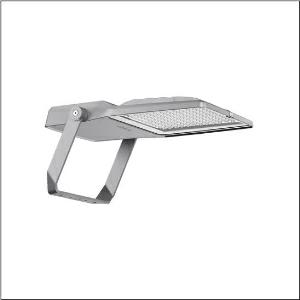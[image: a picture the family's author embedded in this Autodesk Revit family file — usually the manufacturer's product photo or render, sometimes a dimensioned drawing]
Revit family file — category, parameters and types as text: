
# Revit family: floodlight_fl_21_iq_midi___rs07_5xa7782f1b1a_00ed
name_source: partatom
category: Lighting Fixtures
units: mm (PartAtom-declared; Revit-internal decimal feet)

## family parameters
Cut with Voids When Loaded = No
Host = Face
Light Source = No
Part Type = Normal
Room Calculation Point = No
Round Connector Dimension = Use Diameter
Shared = No

## types (1)
- --- (1 x LED, 29450 lm, 270.2 W, 2200K)
    Apparent Load = 270 VA
    CIE Flux Codes = 79 92 99 100 100
    Color Rendering = 70
    Color Temperature = 2200K
    Default Elevation = 1800 mm
    Description = Floodlight FL 21 iQ midi, floodlight, primary light control with lens, of PMMA, primary optical cover: protective disc, of toughened safety glass, transparent, light distribution: RS07, light emission: direct distribution, installation type: surface-mounted, LED, High Power LED, rated luminous flux: 29.450lm, luminous efficacy: 109lm/W, light colour: 722, colour temperature: 2200K, control gear: ECG iQ, control: optimised constant luminous flux control (CLO 2.0), Desk-Remote (wireless, voltage-free reading and setting of iQ features in the workshop via application-optimized NFC function/RFID function), Smart-Wire, Night-Set, Temp-Guard, Street-Remote, Auto-Match, with terminal, 6-pole, mains connection: 220..240V, AC, 50/60Hz, start of lifetime: 270W, end of service life: 287W, reduction: 117W, luminaire housing, of diecast aluminium, powder-coated, Siteco® metallic grey (DB 702S), corrosivity category C5 mid according to DIN EN ISO 12944, sealing non-destructively replaceable, mounting bracket, of steel, galvanised, powder-coated, Siteco® metallic grey (DB 702S), protection rating (complete): IP66, insulation class (complete): insulation class II (safety insulation), certification: CE, protection symbol: D, impact resistance: IK08, permissible operating ambient temperature: -40..+40°C, permissible operating ambient temperature for outdoor applications: -40..+50°C, standard: DIN EN 12944, LABS conformity tested according to VDMA 24364:2018-05, packaging unit: 1 piece

Light Distribution: RS07
    Height = 76 mm
    Lamp = 1 x LED
    Lamp Light Flux = 29450 lm
    Lamp Power = 270.2 W
    Lamp count = 1
    Length = 657 mm
    Luminous efficacy = 109 lm/W
    Manufacturer = Siteco
    ModVariant = No
    Model = 5XA7782F1B1A
    Number of Poles = 1
    OnlyDefault = Yes
    Power Factor = 1
    Product Name = Floodlight FL 21 iQ midi | RS07
    Product group = floodlight | pylon annexe
    ProductGroupID = 6200
    Protection Class = Protection class II
    Protection Degree = IP 66
    RLX_Detail_Level = 1
    RLX_Emergency_Light_Flux = 0 lm
    RLX_Emergency_Type = 0
    RLX_Emergency_Type_DB = No
    RlxData = <blob elided: 141341 chars, md5=8ae6870e>
    Socket = socket
    Standby Power = 0 W
    System Light Flux = 29450 lm
    System Power = 270 W
    Type Comments = factory setting: luminous flux: 100 % | dim-lin: 254 | 620 mA
    Type Image = l_1006876.jpg
    URL = http://relux.com
    VarID = @adj_037679
    Voltage = 0 V
    Weight = 0.00 kg
    Width = 442 mm

## geometry (parser evidence)
native form markers: Blend x4, Sweep x14
no freeform markers — native parametric forms only
